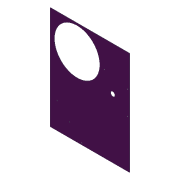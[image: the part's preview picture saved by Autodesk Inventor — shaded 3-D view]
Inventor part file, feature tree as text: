
AUTODESK INVENTOR PART (.ipt)
format: ipt  version: 2012 (Build 160160000, 160)  size: 125,952 bytes
history: native  units: in
note: dims shown in document units (in); Inventor stores cm internally (conversion verified against a paired STEP export)
features: extrude x4, sketch x4
ambient origin geometry x8: Origin, YZ Plane, XZ Plane, XY Plane, X Axis, Y Axis, Z Axis, Center Point
bodies: Solid1 (feature_tree)
feature tree (8):
  extrude  "Extrusion1"  Depth=26.0in
  extrude  "Extrusion2"  Depth=10.0in
  extrude  "Extrusion10"  Depth=11.5in
  extrude  "Extrusion11"  Depth=6.75in
  sketch  "Sketch1"  dims[d0=20.0in d1=26.0in]
  sketch  "Sketch2"  dims[d2=13.0in d3=10.0in]
  sketch  "Sketch10"  dims[d4=0.0625in d5=0.0in d6=11.5in]
  sketch  "Sketch11"  dims[d7=6.25in d8=6.75in d11=7.5in d12=11.0in d14=30.0in d16=6.0in d19=3.0in d23=1.125in d24=3.6875in d25=0.0in d27=11.0in d28=1.0in d29=0.25in d31=15.0in d33=0.25in d34=0.25in d208=0.25in d210=0.5in d212=1.0in d213=0.0in d214=6.0in d215=4.25in d216=6.25in d217=6.25in d218=0.25in d219=1.5in d220=1.0in d221=1.0in d222=0.0in]
